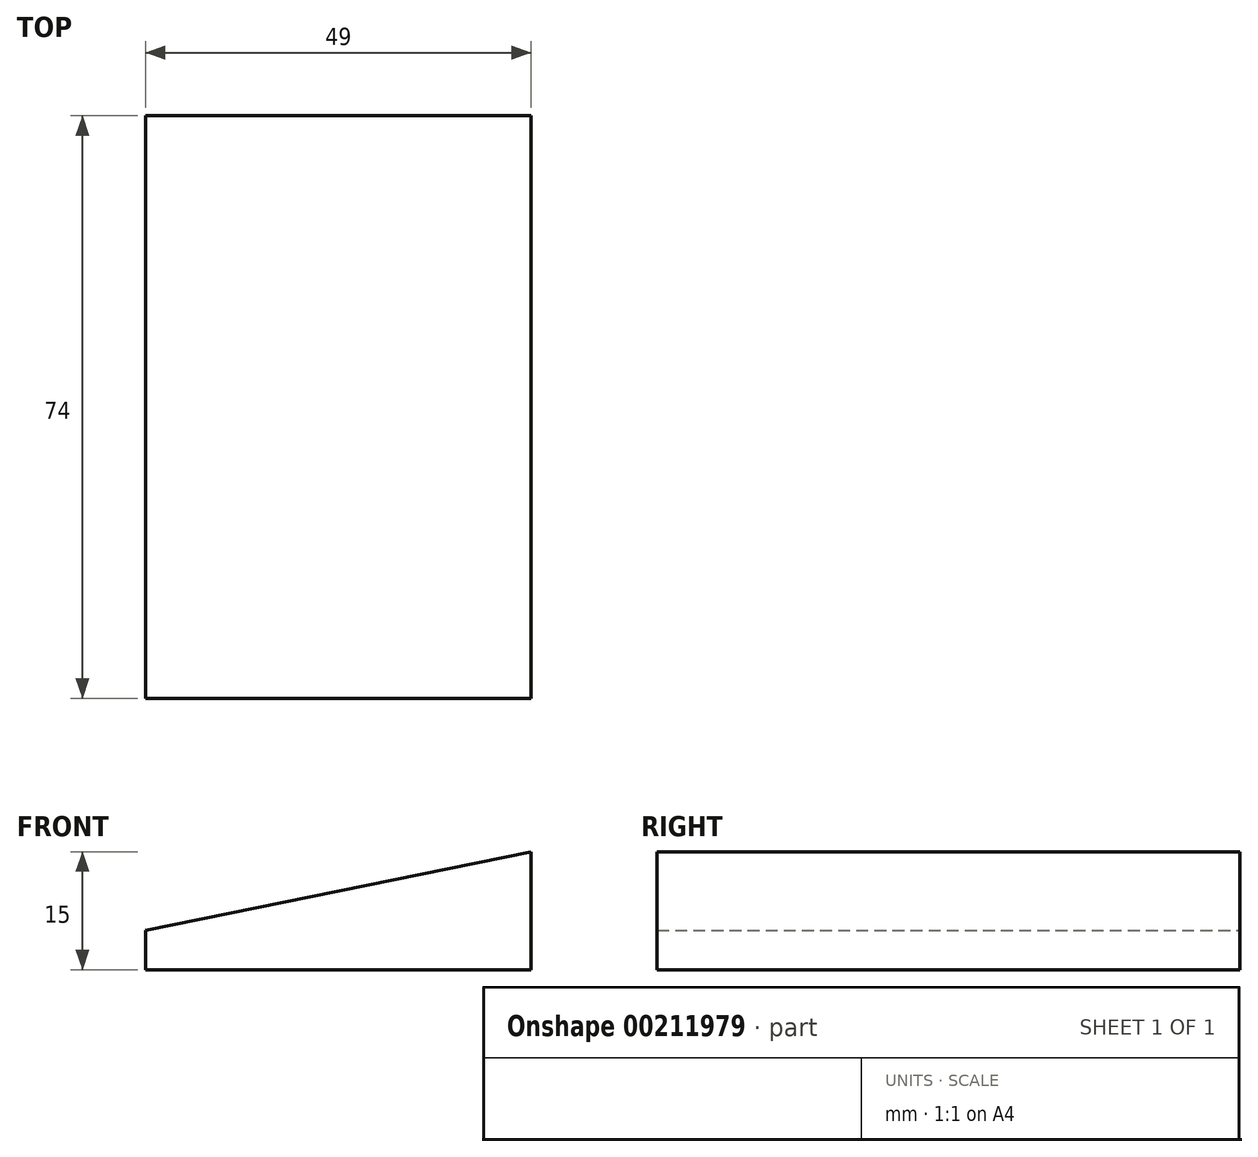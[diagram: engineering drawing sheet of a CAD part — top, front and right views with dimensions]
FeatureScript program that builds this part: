
annotation { "Feature Type Name" : "Feature", "Feature Type Description" : "" }
export const myFeature = defineFeature(function(context is Context, id is Id, definition is map)
    precondition{}
    {
        {
            var Q0;
            Q0=qCreatedBy(makeId("Front.planeOp"),FACE);
            var sketch = newSketch(context, id + "F0", { "sketchPlane" : qUnion([Q0])});
            skLineSegment(sketch, "E0", {"start": v(-12.16, 0) * mm, "end": v(36.84, 0) * mm});
            skLineSegment(sketch, "E1", {"start": v(36.84, 0) * mm, "end": v(36.84, 15) * mm});
            skLineSegment(sketch, "E2", {"start": v(36.84, 15) * mm, "end": v(-12.16, 5) * mm});
            skLineSegment(sketch, "E3", {"start": v(-12.16, 0) * mm, "end": v(-12.16, 5) * mm});
            skSolve(sketch);
        }
        {
            var Q0;
            Q0=makeQuery(id+"F0.imprint","IMPRINT",FACE,{"disambiguationData":[TD([[makeQuery(id+"F0.imprint","IMPRINT",EDGE,{"derivedFrom":sQuery(id+"F0.wireOp",EDGE,"E0")}),1.0]])]});
            extrude(context, id + "F1", {"entities" : qUnion([Q0]), "depth" : (80 - 6) * mm});
        }
    });
